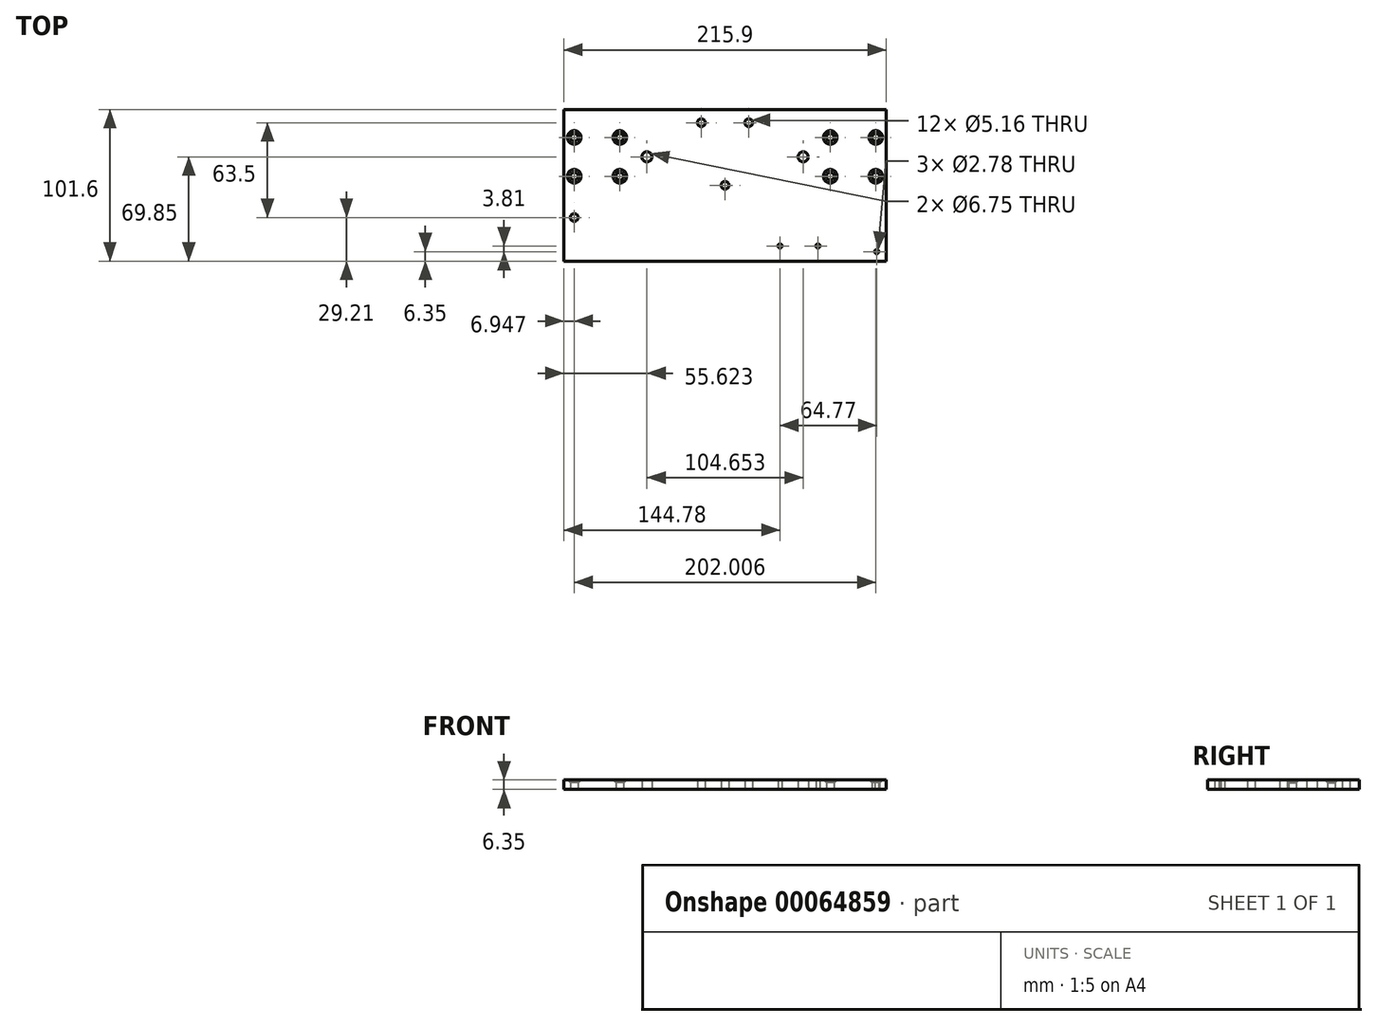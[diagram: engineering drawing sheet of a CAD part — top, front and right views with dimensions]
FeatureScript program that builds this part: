
annotation { "Feature Type Name" : "Feature", "Feature Type Description" : "" }
export const myFeature = defineFeature(function(context is Context, id is Id, definition is map)
    precondition{}
    {
        {
            var Q0;
            Q0=qCreatedBy(makeId("Top.planeOp"),FACE);
            var sketch = newSketch(context, id + "F0", { "sketchPlane" : qUnion([Q0])});
            skLineSegment(sketch, "E0.rect.bottom", {"start": v(107.95, 50.8) * mm, "end": v(-107.95, 50.8) * mm});
            skLineSegment(sketch, "E0.rect.top", {"start": v(107.95, -50.8) * mm, "end": v(-107.95, -50.8) * mm});
            skLineSegment(sketch, "E0.rect.left", {"start": v(107.95, 50.8) * mm, "end": v(107.95, -50.8) * mm});
            skLineSegment(sketch, "E0.rect.right", {"start": v(-107.95, 50.8) * mm, "end": v(-107.95, -50.8) * mm});
            skPoint(sketch, "E0.rect.middle", {"position": v(0, 0) * mm});
            skCircle(sketch, "E1", {"center": v(0, 0) * mm, "radius": 2.58 * mm});
            skCircle(sketch, "E2", {"center": v(-101, 32.04) * mm, "radius": 2.58 * mm});
            skCircle(sketch, "E3", {"center": v(-70.45, 32.04) * mm, "radius": 2.58 * mm});
            skCircle(sketch, "E4", {"center": v(-70.45, 6.06) * mm, "radius": 2.58 * mm});
            skCircle(sketch, "E5", {"center": v(-101, 6.06) * mm, "radius": 2.58 * mm});
            skCircle(sketch, "E6", {"center": v(-101, -21.6) * mm, "radius": 2.58 * mm});
            skCircle(sketch, "E7", {"center": v(-52.33, 19.05) * mm, "radius": 3.37 * mm});
            skCircle(sketch, "E8", {"center": v(-15.88, 41.91) * mm, "radius": 2.58 * mm});
            skCircle(sketch, "E9", {"center": v(101.6, -44.45) * mm, "radius": 1.39 * mm});
            skLineSegment(sketch, "E10", {"start": v(0, 0) * mm, "end": v(0, 66.65) * mm, "construction": true});
            skPoint(sketch, "E10.endSnap0", {"position": v(0, 50.8) * mm});
            skCircle(sketch, "E11.MirrorC", {"center": v(101, 32.04) * mm, "radius": 2.58 * mm});
            skCircle(sketch, "E12.MirrorC", {"center": v(101, 6.06) * mm, "radius": 2.58 * mm});
            skCircle(sketch, "E13.MirrorC", {"center": v(70.45, 6.06) * mm, "radius": 2.58 * mm});
            skCircle(sketch, "E14.MirrorC", {"center": v(70.45, 32.04) * mm, "radius": 2.58 * mm});
            skCircle(sketch, "E15.MirrorC", {"center": v(52.33, 19.05) * mm, "radius": 3.37 * mm});
            skCircle(sketch, "E16.MirrorC", {"center": v(15.88, 41.91) * mm, "radius": 2.58 * mm});
            skCircle(sketch, "E17", {"center": v(36.83, -40.64) * mm, "radius": 1.39 * mm});
            skCircle(sketch, "E18", {"center": v(62.23, -40.64) * mm, "radius": 1.39 * mm});
            skSolve(sketch);
        }
        {
            var Q0;
            Q0=makeQuery(id+"F0.imprint","IMPRINT",FACE,{"disambiguationData":[TD([[makeQuery(id+"F0.imprint","IMPRINT",EDGE,{"derivedFrom":sQuery(id+"F0.wireOp",EDGE,"E0.rect.bottom")}),1.0]])]});
            extrude(context, id + "F1", {"entities" : qUnion([Q0]), "depth" : 6.35 * mm});
        }
        {
            var Q0;
            Q0=makeQuery(id+"F1.opExtrude","CAP_EDGE",EDGE,{"disambiguationData":[OSD([sQuery(id+"F0.wireOp",EDGE,"E3")])],"isStart":false});
            var Q1;
            Q1=makeQuery(id+"F1.opExtrude","CAP_EDGE",EDGE,{"disambiguationData":[OSD([sQuery(id+"F0.wireOp",EDGE,"E2")])],"isStart":false});
            var Q2;
            Q2=makeQuery(id+"F1.opExtrude","CAP_EDGE",EDGE,{"disambiguationData":[OSD([sQuery(id+"F0.wireOp",EDGE,"E5")])],"isStart":false});
            var Q3;
            Q3=makeQuery(id+"F1.opExtrude","CAP_EDGE",EDGE,{"disambiguationData":[OSD([sQuery(id+"F0.wireOp",EDGE,"E4")])],"isStart":false});
            var Q4;
            Q4=makeQuery(id+"F1.opExtrude","CAP_EDGE",EDGE,{"disambiguationData":[OSD([sQuery(id+"F0.wireOp",EDGE,"E14.MirrorC")])],"isStart":false});
            var Q5;
            Q5=makeQuery(id+"F1.opExtrude","CAP_EDGE",EDGE,{"disambiguationData":[OSD([sQuery(id+"F0.wireOp",EDGE,"E13.MirrorC")])],"isStart":false});
            var Q6;
            Q6=makeQuery(id+"F1.opExtrude","CAP_EDGE",EDGE,{"disambiguationData":[OSD([sQuery(id+"F0.wireOp",EDGE,"E12.MirrorC")])],"isStart":false});
            var Q7;
            Q7=makeQuery(id+"F1.opExtrude","CAP_EDGE",EDGE,{"disambiguationData":[OSD([sQuery(id+"F0.wireOp",EDGE,"E11.MirrorC")])],"isStart":false});
            chamfer(context, id + "F2", {"entities" : qUnion([Q0, Q1, Q2, Q3, Q4, Q5, Q6, Q7]), "width" : 1.98 * mm, "tangentPropagation" : true});
        }
    });
